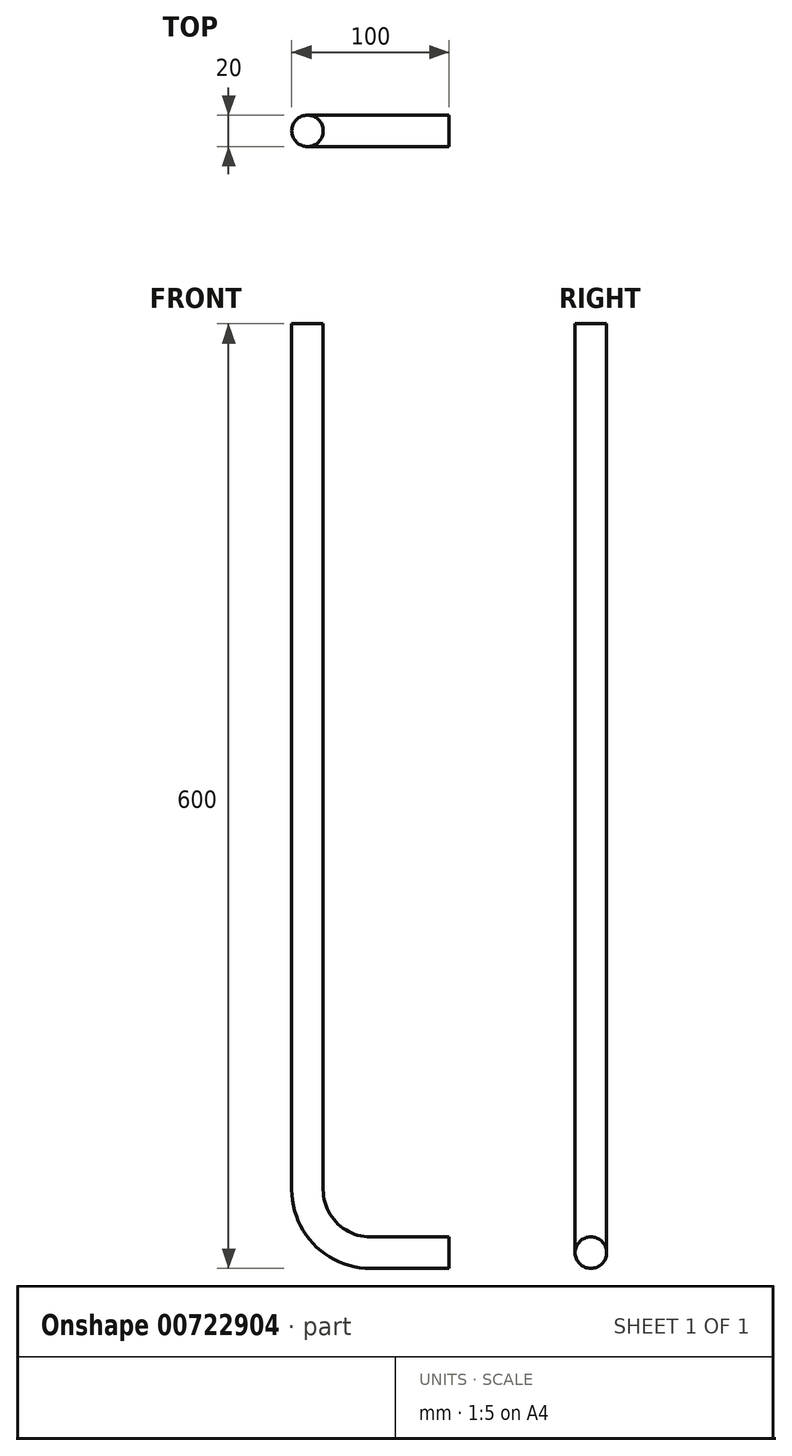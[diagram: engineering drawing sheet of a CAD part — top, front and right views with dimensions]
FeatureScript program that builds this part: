
annotation { "Feature Type Name" : "Feature", "Feature Type Description" : "" }
export const myFeature = defineFeature(function(context is Context, id is Id, definition is map)
    precondition{}
    {
        {
            var Q0;
            Q0=qCreatedBy(makeId("Front.planeOp"),FACE);
            var sketch = newSketch(context, id + "F0", { "sketchPlane" : qUnion([Q0])});
            skLineSegment(sketch, "E0", {"start": v(0, 50) * mm, "end": v(0, 600) * mm});
            skLineSegment(sketch, "E1", {"start": v(50, 0) * mm, "end": v(100, 0) * mm});
            skPoint(sketch, "E2.visualSharp", {"position": v(0, 0) * mm});
            skArc(sketch, "E2.filletArc", {"start": v(0, 50) * mm, "mid": v(14.64, 14.64) * mm, "end": v(50, 0) * mm});
            skLineSegment(sketch, "E3.0", {"start": v(20, 50) * mm, "end": v(20, 600) * mm});
            skArc(sketch, "E3.1", {"start": v(20, 50) * mm, "mid": v(28.79, 28.79) * mm, "end": v(50, 20) * mm});
            skLineSegment(sketch, "E3.2", {"start": v(50, 20) * mm, "end": v(100, 20) * mm});
            skLineSegment(sketch, "E4", {"start": v(0, 600) * mm, "end": v(20, 600) * mm});
            skLineSegment(sketch, "E5", {"start": v(100, 20) * mm, "end": v(100, 0) * mm});
            skSolve(sketch);
        }
        {
            var Q0;
            Q0=makeQuery(id+"F0.imprint","IMPRINT",FACE,{"disambiguationData":[TD([[makeQuery(id+"F0.imprint","IMPRINT",EDGE,{"derivedFrom":sQuery(id+"F0.wireOp",EDGE,"E0")}),-1.0]])]});
            extrude(context, id + "F1", {"entities" : qUnion([Q0]), "depth" : 20 * mm, "offsetDistance" : 25 * mm});
        }
        {
            var Q0;
            Q0=makeQuery(id+"F1.opExtrude","CAP_EDGE",EDGE,{"disambiguationData":[OSD([sQuery(id+"F0.wireOp",EDGE,"E0")])],"isStart":false});
            var Q1;
            Q1=makeQuery(id+"F1.opExtrude","CAP_EDGE",EDGE,{"disambiguationData":[OSD([sQuery(id+"F0.wireOp",EDGE,"E3.0")])],"isStart":false});
            var Q2;
            Q2=makeQuery(id+"F1.opExtrude","CAP_EDGE",EDGE,{"disambiguationData":[OSD([sQuery(id+"F0.wireOp",EDGE,"E3.0")])],"isStart":true});
            var Q3;
            Q3=makeQuery(id+"F1.opExtrude","CAP_EDGE",EDGE,{"disambiguationData":[OSD([sQuery(id+"F0.wireOp",EDGE,"E0")])],"isStart":true});
            fillet(context, id + "F2", {"entities" : qUnion([Q0, Q1, Q2, Q3]), "radius" : 10 * mm, "tangentPropagation" : true, "allowEdgeOverflow" : false});
        }
    });
